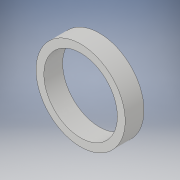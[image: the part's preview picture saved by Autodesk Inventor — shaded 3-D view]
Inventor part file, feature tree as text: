
AUTODESK INVENTOR PART (.ipt)
format: ipt  version: 2019 (Build 230136000, 136)  size: 103,936 bytes
history: native  units: mm
features: extrude x2, sketch x2
ambient origin geometry x8: Origin, YZ Plane, XZ Plane, XY Plane, X Axis, Y Axis, Z Axis, Center Point
bodies: Solid1 (feature_tree)
feature tree (4):
  extrude  "Extrusion1"  Depth=60.0mm TaperAngle=0.0deg
  extrude  "Extrusion2"  Depth=6.0mm TaperAngle=0.0deg
  sketch  "Sketch1"  dims[d0=285.0mm d1=60.0mm d2=0.0mm]
  sketch  "Sketch2"  dims[d3=235.0mm d4=6.0mm d5=0.0mm]
